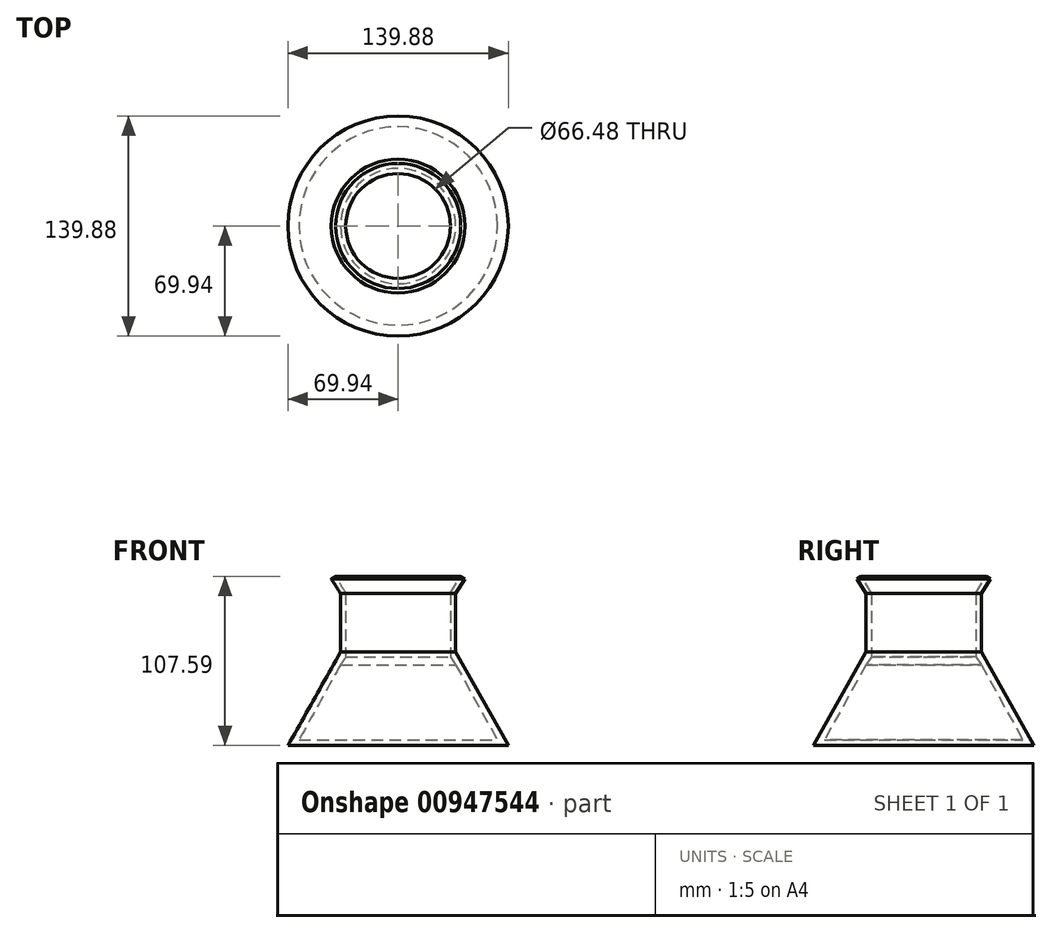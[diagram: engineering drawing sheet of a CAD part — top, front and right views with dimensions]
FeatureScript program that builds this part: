
annotation { "Feature Type Name" : "Feature", "Feature Type Description" : "" }
export const myFeature = defineFeature(function(context is Context, id is Id, definition is map)
    precondition{}
    {
        {
            var Q0;
            Q0=qCreatedBy(makeId("Right.planeOp"),FACE);
            var sketch = newSketch(context, id + "F0", { "sketchPlane" : qUnion([Q0])});
            skLineSegment(sketch, "E0", {"start": v(-42.47, 49.7) * mm, "end": v(-36.6, 40.48) * mm});
            skLineSegment(sketch, "E1", {"start": v(-36.6, 40.48) * mm, "end": v(-36.6, 3.15) * mm});
            skLineSegment(sketch, "E2", {"start": v(-36.6, 3.15) * mm, "end": v(-69.94, -56.2) * mm});
            skLineSegment(sketch, "E3", {"start": v(-69.94, -56.2) * mm, "end": v(0, -56.2) * mm});
            skLineSegment(sketch, "E4", {"start": v(0, -56.2) * mm, "end": v(0, -52.64) * mm});
            skLineSegment(sketch, "E5", {"start": v(0, -52.64) * mm, "end": v(-63.02, -52.64) * mm});
            skLineSegment(sketch, "E6", {"start": v(-63.02, -52.64) * mm, "end": v(-36.6, -4.82) * mm});
            skLineSegment(sketch, "E7", {"start": v(-36.6, -4.82) * mm, "end": v(-33.24, 0) * mm});
            skLineSegment(sketch, "E8", {"start": v(-33.24, 0) * mm, "end": v(-33.24, 40.69) * mm});
            skLineSegment(sketch, "E9", {"start": v(-33.24, 40.69) * mm, "end": v(-39.74, 51.38) * mm});
            skLineSegment(sketch, "E10", {"start": v(-39.74, 51.38) * mm, "end": v(-42.47, 49.7) * mm});
            skLineSegment(sketch, "E11", {"start": v(-48.71, -18.42) * mm, "end": v(-65.12, -11.53) * mm});
            skLineSegment(sketch, "E12", {"start": v(-65.12, -11.53) * mm, "end": v(-58.46, -35.77) * mm});
            skLineSegment(sketch, "E13", {"start": v(-58.46, -35.77) * mm, "end": v(-73.3, -32.09) * mm});
            skLineSegment(sketch, "E14", {"start": v(-73.3, -32.09) * mm, "end": v(-68.23, -53.16) * mm});
            skSolve(sketch);
        }
        {
            var Q0;
            Q0=makeQuery(id+"F0.imprint","IMPRINT",FACE,{"disambiguationData":[TD([[makeQuery(id+"F0.imprint","IMPRINT",EDGE,{"derivedFrom":sQuery(id+"F0.wireOp",EDGE,"E0")}),1.0]])]});
            var Q1;
            Q1=sQuery(id+"F0.wireOp",EDGE,"E4");
            revolve(context, id + "F1", {"surfaceOperationType" : NewSurfaceOperationType.NEW, "entities" : qUnion([Q0]), "axis" : qUnion([Q1]), "revolveType" : RevolveType.FULL});
        }
    });
